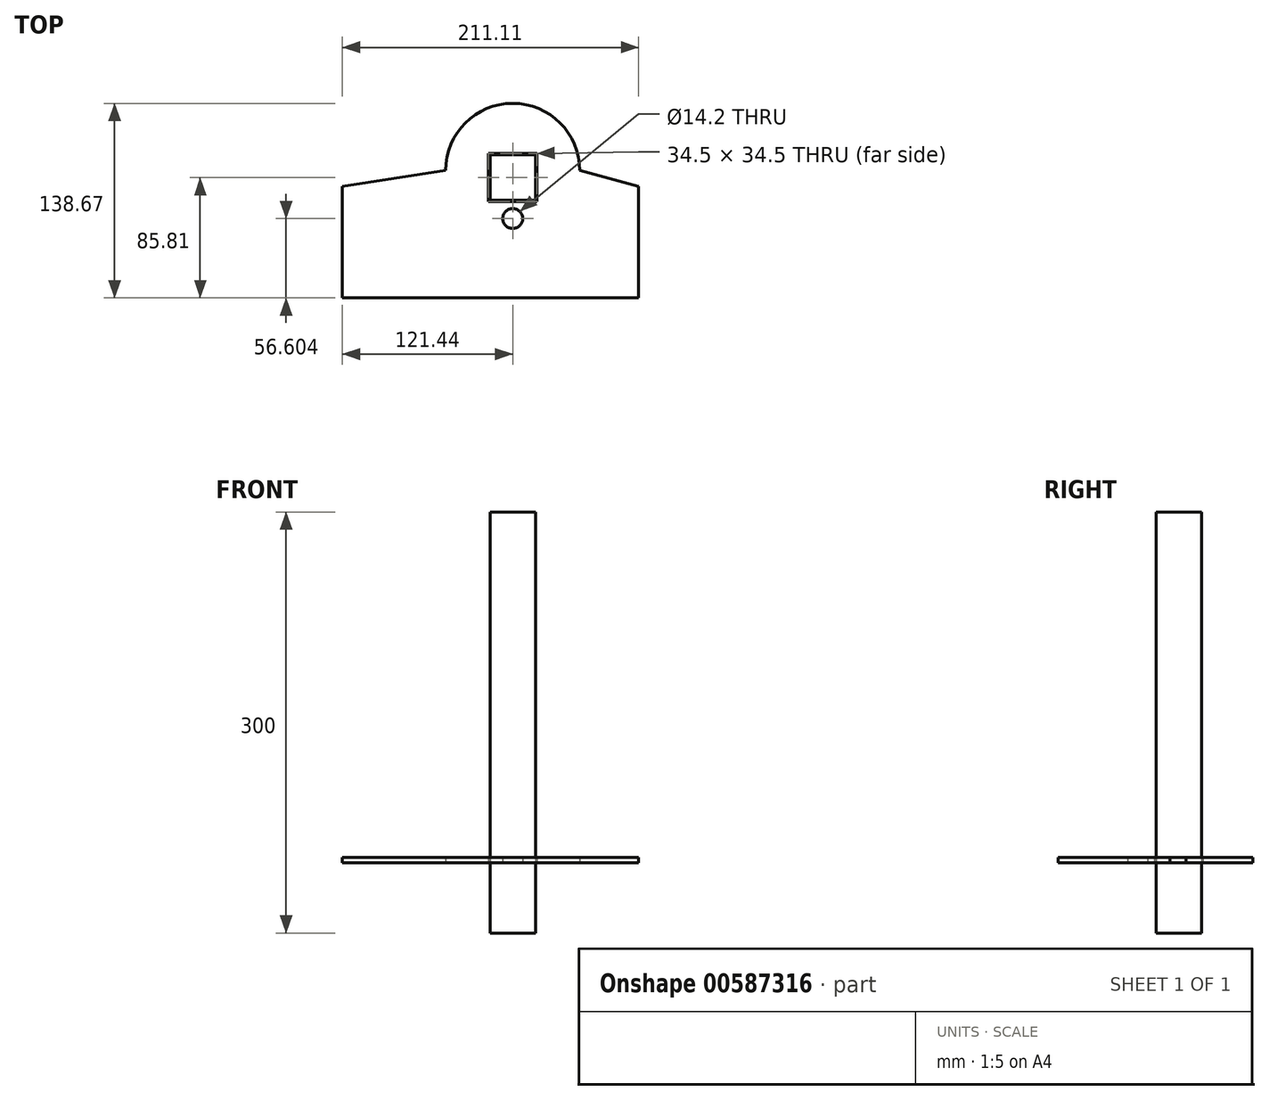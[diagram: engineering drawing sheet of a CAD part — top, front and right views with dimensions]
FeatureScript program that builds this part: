
annotation { "Feature Type Name" : "Feature", "Feature Type Description" : "" }
export const myFeature = defineFeature(function(context is Context, id is Id, definition is map)
    precondition{}
    {
        {
            var Q0;
            Q0=qCreatedBy(makeId("Top.planeOp"),FACE);
            var sketch = newSketch(context, id + "F0", { "sketchPlane" : qUnion([Q0]) });
            skLineSegment(sketch, "E0.bottom", {"start": v(-16.25, 16.25) * mm, "end": v(16.25, 16.25) * mm});
            skLineSegment(sketch, "E0.top", {"start": v(-16.25, -16.25) * mm, "end": v(16.25, -16.25) * mm});
            skLineSegment(sketch, "E0.left", {"start": v(-16.25, 16.25) * mm, "end": v(-16.25, -16.25) * mm});
            skLineSegment(sketch, "E0.right", {"start": v(16.25, 16.25) * mm, "end": v(16.25, -16.25) * mm});
            skPoint(sketch, "E0.middle", {"position": v(0, 0) * mm});
            skSolve(sketch);
        }
        {
            var Q0;
            Q0 = qSketchRegion(id + "F0", true);
            var Q1;
            Q1=sQuery(id+"F0.wireOp",EDGE,"E0.bottom");
            extrude(context, id + "F1", {"entities" : qUnion([Q0]), "surfaceEntities" : qUnion([Q1]), "endBound" : BoundingType.SYMMETRIC, "depth" : 300 * mm, "offsetDistance" : 25 * mm});
        }
        {
            var Q0;
            Q0=qCreatedBy(makeId("Top.planeOp"),FACE);
            cPlane(context, id + "F2", {"entities" : qUnion([Q0]), "cplaneType" : CPlaneType.OFFSET, "offset" : 100 * mm, "oppositeDirection" : true, "width" : 150 * mm, "height" : 150 * mm});
        }
        {
            var Q0;
            Q0=qCreatedBy(id+"F2.planeOp",FACE);
            var sketch = newSketch(context, id + "F3", { "sketchPlane" : qUnion([Q0]) });
            skLineSegment(sketch, "E1.0", {"start": v(-16.25, 16.25) * mm, "end": v(16.25, 16.25) * mm, "construction": true});
            skLineSegment(sketch, "E1.1", {"start": v(16.25, 16.25) * mm, "end": v(16.25, -16.25) * mm, "construction": true});
            skLineSegment(sketch, "E1.2", {"start": v(-16.25, -16.25) * mm, "end": v(16.25, -16.25) * mm, "construction": true});
            skLineSegment(sketch, "E1.3", {"start": v(-16.25, 16.25) * mm, "end": v(-16.25, -16.25) * mm, "construction": true});
            skLineSegment(sketch, "E2.bottom", {"start": v(17.25, -17.25) * mm, "end": v(-17.25, -17.25) * mm});
            skLineSegment(sketch, "E2.top", {"start": v(17.25, 17.25) * mm, "end": v(-17.25, 17.25) * mm});
            skLineSegment(sketch, "E2.left", {"start": v(17.25, -17.25) * mm, "end": v(17.25, 17.25) * mm});
            skLineSegment(sketch, "E2.right", {"start": v(-17.25, -17.25) * mm, "end": v(-17.25, 17.25) * mm});
            skPoint(sketch, "E2.middle", {"position": v(0, 0) * mm});
            skArc(sketch, "E3", {"start": v(47.75, 5.11) * mm, "mid": v(0, 52.86) * mm, "end": v(-47.75, 5.11) * mm});
            skPoint(sketch, "E4", {"position": v(0, 17.25) * mm});
            skLineSegment(sketch, "E5", {"start": v(-47.75, 5.11) * mm, "end": v(47.75, 5.11) * mm, "construction": true});
            skCircle(sketch, "E6", {"center": v(0, -29.2) * mm, "radius": 7.1 * mm});
            skLineSegment(sketch, "E7.bottom", {"start": v(-121.44, -6.32) * mm, "end": v(89.67, -6.32) * mm});
            skLineSegment(sketch, "E7.top", {"start": v(-121.44, -85.81) * mm, "end": v(89.67, -85.81) * mm});
            skLineSegment(sketch, "E7.left", {"start": v(-121.44, -6.32) * mm, "end": v(-121.44, -85.81) * mm});
            skLineSegment(sketch, "E7.right", {"start": v(89.67, -6.32) * mm, "end": v(89.67, -85.81) * mm});
            skLineSegment(sketch, "E8", {"start": v(-47.75, 5.11) * mm, "end": v(-121.44, -6.32) * mm});
            skLineSegment(sketch, "E9", {"start": v(47.75, 5.11) * mm, "end": v(89.67, -6.32) * mm});
            skSolve(sketch);
        }
        {
            var Q0;
            Q0 = qSketchRegion(id + "F3", true);
            extrude(context, id + "F4", {"entities" : qUnion([Q0]), "depth" : 4 * mm, "offsetDistance" : 25 * mm});
        }
    });
